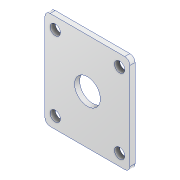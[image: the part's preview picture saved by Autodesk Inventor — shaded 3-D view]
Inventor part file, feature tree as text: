
AUTODESK INVENTOR PART (.ipt)
format: ipt  version: 2020 (Build 240168000, 168)  size: 121,344 bytes
history: native  units: mm
features: extrude x2, sketch x2, other x1, fillet x1
ambient origin geometry x8: Origin, YZ Plane, XZ Plane, XY Plane, X Axis, Y Axis, Z Axis, Center Point
bodies: Body1 (feature_tree)
feature tree (6):
  other  "솔리드1"
  extrude  "돌출1"  Depth=2.0mm TaperAngle=0.0deg
  fillet  "모깎기1"  Radius=2.0mm
  extrude  "돌출2"  Depth=10.0mm
  sketch  "스케치1"
  sketch  "스케치2"
